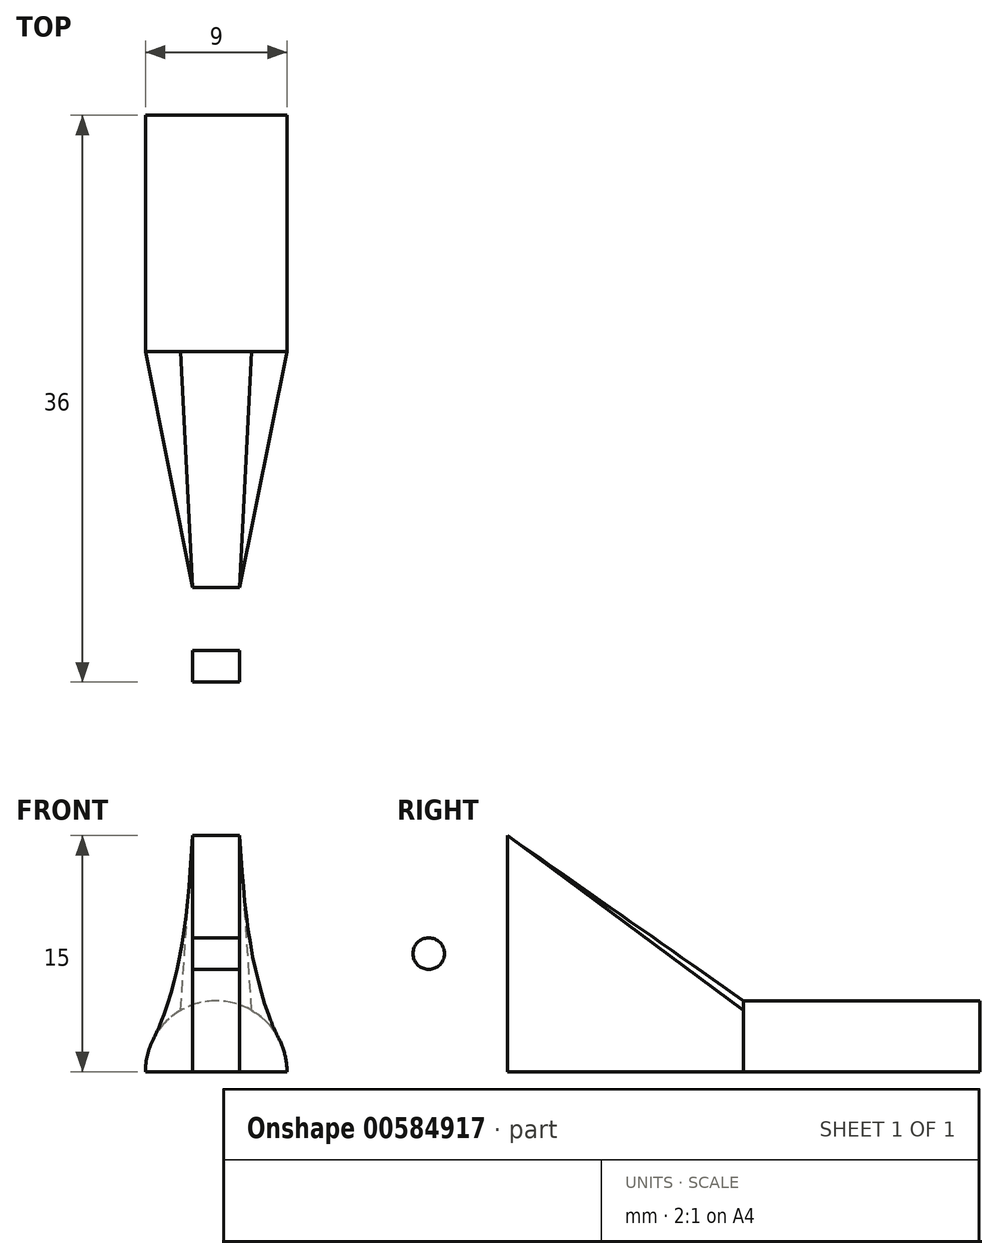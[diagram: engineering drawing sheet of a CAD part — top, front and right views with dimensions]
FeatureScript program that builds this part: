
annotation { "Feature Type Name" : "Feature", "Feature Type Description" : "" }
export const myFeature = defineFeature(function(context is Context, id is Id, definition is map)
    precondition{}
    {
        {
            var Q0;
            Q0=qCreatedBy(makeId("Front.planeOp"),FACE);
            var sketch = newSketch(context, id + "F0", { "sketchPlane" : qUnion([Q0])});
            skArc(sketch, "E0", {"start": v(4.5, 0) * mm, "mid": v(0, 4.5) * mm, "end": v(-4.5, 0) * mm});
            skLineSegment(sketch, "E1", {"start": v(-4.5, 0) * mm, "end": v(4.5, 0) * mm});
            skSolve(sketch);
        }
        {
            var Q0;
            Q0=makeQuery(id+"F0.imprint","IMPRINT",FACE,{"disambiguationData":[TD([[makeQuery(id+"F0.imprint","IMPRINT",EDGE,{"derivedFrom":sQuery(id+"F0.wireOp",EDGE,"E0")}),1.0]])]});
            extrude(context, id + "F1", {"entities" : qUnion([Q0]), "depth" : 15 * mm, "offsetDistance" : 25 * mm});
        }
        {
            var Q0;
            Q0=qCreatedBy(makeId("Front.planeOp"),FACE);
            cPlane(context, id + "F2", {"entities" : qUnion([Q0]), "cplaneType" : CPlaneType.OFFSET, "offset" : 30 * mm, "width" : 150 * mm, "height" : 150 * mm});
        }
        {
            var Q0;
            Q0=qCreatedBy(id+"F2.planeOp",FACE);
            var sketch = newSketch(context, id + "F3", { "sketchPlane" : qUnion([Q0])});
            skLineSegment(sketch, "E2.bottom", {"start": v(-1.5, 0) * mm, "end": v(1.5, 0) * mm});
            skLineSegment(sketch, "E2.top", {"start": v(-1.5, 15) * mm, "end": v(1.5, 15) * mm});
            skLineSegment(sketch, "E2.left", {"start": v(-1.5, 0) * mm, "end": v(-1.5, 15) * mm});
            skLineSegment(sketch, "E2.right", {"start": v(1.5, 0) * mm, "end": v(1.5, 15) * mm});
            skSolve(sketch);
        }
        {
            var Q1;
            Q1=makeQuery(id+"F1.opExtrude","CAP_FACE",FACE,{"disambiguationData":[OSD([sQuery(id+"F0.wireOp",EDGE,"E0"),sQuery(id+"F0.wireOp",EDGE,"E1")])],"isStart":false});
            var Q2;
            Q2=makeQuery(id+"F3.imprint","IMPRINT",FACE,{"disambiguationData":[TD([[makeQuery(id+"F3.imprint","IMPRINT",EDGE,{"derivedFrom":sQuery(id+"F3.wireOp",EDGE,"E2.bottom")}),1.0]])]});
            loft(context, id + "F4", {"operationType" : NewBodyOperationType.ADD, "sheetProfilesArray" : [{ "sheetProfileEntities" : qUnion([Q1]) }, { "sheetProfileEntities" : qUnion([Q2]) }]});
        }
        {
            var Q0;
            Q0=makeQuery(id+"F4.opLoft","CAP_FACE",FACE,{"disambiguationData":[OSD([makeQuery(id+"F3.imprint","IMPRINT",FACE,{"disambiguationData":[TD([[makeQuery(id+"F3.imprint","IMPRINT",EDGE,{"derivedFrom":sQuery(id+"F3.wireOp",EDGE,"E2.bottom")}),1.0]])]})])],"isStart":true});
            extrude(context, id + "F5", {"entities" : qUnion([Q0]), "operationType" : NewBodyOperationType.ADD, "depth" : 25 * mm, "offsetDistance" : 25 * mm});
        }
        {
            var Q0;
            Q0=makeQuery(id+"F5.opExtrude","SWEPT_FACE",FACE,{"disambiguationData":[OSD([sQuery(id+"F3.wireOp",EDGE,"E2.bottom"),sQuery(id+"F3.wireOp",EDGE,"E2.top"),sQuery(id+"F3.wireOp",EDGE,"E2.right")])]});
            var sketch = newSketch(context, id + "F6", { "sketchPlane" : qUnion([Q0])});
            skCircle(sketch, "E3", {"center": v(-50, 7.5) * mm, "radius": 1 * mm});
            skLineSegment(sketch, "E4", {"start": v(-55, 7.5) * mm, "end": v(-30, 7.5) * mm, "construction": true});
            skLineSegment(sketch, "E5", {"start": v(-42.5, 0) * mm, "end": v(-42.5, 15) * mm, "construction": true});
            skFitSpline(sketch, "E6.0", {"points": [v(-55, 0) * mm, v(-46.67, 0) * mm, v(-38.33, 0) * mm, v(-30, 0) * mm], "construction": true});
            skLineSegment(sketch, "E7.0.0", {"start": v(-30, 0) * mm, "end": v(-30, 15) * mm, "construction": true});
            skFitSpline(sketch, "E7.0.1", {"points": [v(-30, 15) * mm, v(-38.33, 15) * mm, v(-46.67, 15) * mm, v(-55, 15) * mm], "construction": true});
            skLineSegment(sketch, "E7.0.2", {"start": v(-55, 15) * mm, "end": v(-55, 0) * mm, "construction": true});
            skFitSpline(sketch, "E7.0.3", {"points": [v(-55, 0) * mm, v(-46.67, 0) * mm, v(-38.33, 0) * mm, v(-30, 0) * mm], "construction": true});
            skCircle(sketch, "E8.MirrorC", {"center": v(-35, 7.5) * mm, "radius": 1 * mm});
            skSolve(sketch);
        }
        {
            var Q0;
            Q0=makeQuery(id+"F6.imprint","IMPRINT",FACE,{"disambiguationData":[TD([[makeQuery(id+"F6.imprint","IMPRINT",EDGE,{"derivedFrom":sQuery(id+"F6.wireOp",EDGE,"E3")}),1.0]])]});
            var Q1;
            Q1=makeQuery(id+"F6.imprint","IMPRINT",FACE,{"disambiguationData":[TD([[makeQuery(id+"F6.imprint","IMPRINT",EDGE,{"derivedFrom":sQuery(id+"F6.wireOp",EDGE,"E8.MirrorC")}),-1.0]])]});
            extrude(context, id + "F7", {"entities" : qUnion([Q0, Q1]), "operationType" : NewBodyOperationType.REMOVE, "endBound" : BoundingType.UP_TO_NEXT, "oppositeDirection" : true, "depth" : 25 * mm, "offsetDistance" : 25 * mm});
        }
    });
